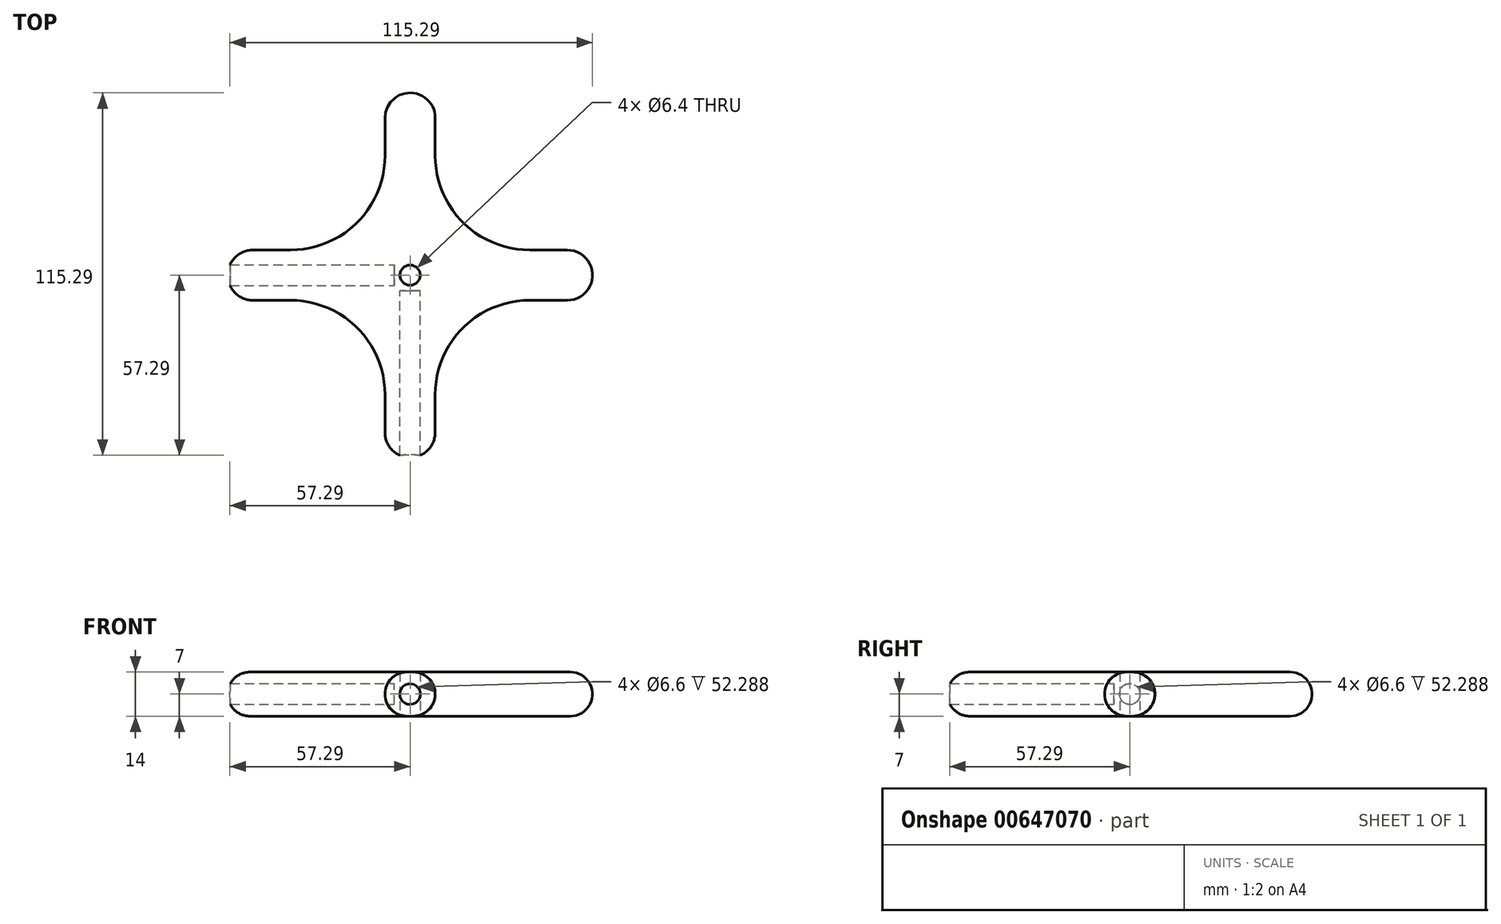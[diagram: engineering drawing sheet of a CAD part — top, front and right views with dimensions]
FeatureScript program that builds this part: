
annotation { "Feature Type Name" : "Feature", "Feature Type Description" : "" }
export const myFeature = defineFeature(function(context is Context, id is Id, definition is map)
    precondition{}
    {
        {
            var Q0;
            Q0=qCreatedBy(makeId("Top.planeOp"),FACE);
            var sketch = newSketch(context, id + "F0", { "sketchPlane" : qUnion([Q0])});
            skCircle(sketch, "E0", {"center": v(0, 0) * mm, "radius": 3.2 * mm});
            skLineSegment(sketch, "E1", {"start": v(0, 58) * mm, "end": v(0, 58) * mm});
            skLineSegment(sketch, "E2", {"start": v(-8, 50) * mm, "end": v(-8, 38) * mm});
            skLineSegment(sketch, "E3", {"start": v(-38, 8) * mm, "end": v(-50, 8) * mm});
            skLineSegment(sketch, "E4", {"start": v(-58, 0) * mm, "end": v(-58, 0) * mm});
            skPoint(sketch, "E5.visualSharp", {"position": v(-8, 8) * mm});
            skArc(sketch, "E5.filletArc", {"start": v(-38, 8) * mm, "mid": v(-16.79, 16.79) * mm, "end": v(-8, 38) * mm});
            skPoint(sketch, "E6.visualSharp", {"position": v(-8, 58) * mm});
            skArc(sketch, "E6.filletArc", {"start": v(0, 58) * mm, "mid": v(-5.66, 55.66) * mm, "end": v(-8, 50) * mm});
            skPoint(sketch, "E7.visualSharp", {"position": v(-58, 8) * mm});
            skArc(sketch, "E7.filletArc", {"start": v(-50, 8) * mm, "mid": v(-55.66, 5.66) * mm, "end": v(-58, 0) * mm});
            skLineSegment(sketch, "E8.MirrorCS", {"start": v(8, 50) * mm, "end": v(8, 38) * mm});
            skArc(sketch, "E9.MirrorCS", {"start": v(38, 8) * mm, "mid": v(16.79, 16.79) * mm, "end": v(8, 38) * mm});
            skArc(sketch, "E10.MirrorCS", {"start": v(0, 58) * mm, "mid": v(5.66, 55.66) * mm, "end": v(8, 50) * mm});
            skLineSegment(sketch, "E11.MirrorCS", {"start": v(38, 8) * mm, "end": v(50, 8) * mm});
            skArc(sketch, "E12.MirrorCS", {"start": v(50, 8) * mm, "mid": v(55.66, 5.66) * mm, "end": v(58, 0) * mm});
            skArc(sketch, "E13.MirrorCS", {"start": v(50, -8) * mm, "mid": v(55.66, -5.66) * mm, "end": v(58, 0) * mm});
            skLineSegment(sketch, "E14.MirrorCS", {"start": v(38, -8) * mm, "end": v(50, -8) * mm});
            skArc(sketch, "E15.MirrorCS", {"start": v(38, -8) * mm, "mid": v(16.79, -16.79) * mm, "end": v(8, -38) * mm});
            skLineSegment(sketch, "E16.MirrorCS", {"start": v(8, -50) * mm, "end": v(8, -38) * mm});
            skArc(sketch, "E17.MirrorCS", {"start": v(0, -58) * mm, "mid": v(5.66, -55.66) * mm, "end": v(8, -50) * mm});
            skArc(sketch, "E18.MirrorCS", {"start": v(0, -58) * mm, "mid": v(-5.66, -55.66) * mm, "end": v(-8, -50) * mm});
            skLineSegment(sketch, "E19.MirrorCS", {"start": v(-8, -50) * mm, "end": v(-8, -38) * mm});
            skArc(sketch, "E20.MirrorCS", {"start": v(-38, -8) * mm, "mid": v(-16.79, -16.79) * mm, "end": v(-8, -38) * mm});
            skLineSegment(sketch, "E21.MirrorCS", {"start": v(-38, -8) * mm, "end": v(-50, -8) * mm});
            skArc(sketch, "E22.MirrorCS", {"start": v(-50, -8) * mm, "mid": v(-55.66, -5.66) * mm, "end": v(-58, 0) * mm});
            skCircle(sketch, "E23", {"center": v(0, 0) * mm, "radius": 30 * mm, "construction": true});
            skSolve(sketch);
        }
        {
            var Q0;
            Q0=makeQuery(id+"F0.imprint","IMPRINT",FACE,{"disambiguationData":[TD([[makeQuery(id+"F0.imprint","IMPRINT",EDGE,{"derivedFrom":sQuery(id+"F0.wireOp",EDGE,"E0")}),-1.0]])]});
            extrude(context, id + "F1", {"entities" : qUnion([Q0]), "depth" : 14 * mm, "offsetDistance" : 25 * mm});
        }
        {
            var Q0;
            Q0=makeQuery(id+"F1.opExtrude","CAP_EDGE",EDGE,{"disambiguationData":[OSD([sQuery(id+"F0.wireOp",EDGE,"E5.filletArc")])],"isStart":false});
            fillet(context, id + "F2", {"entities" : qUnion([Q0]), "radius" : 7 * mm, "tangentPropagation" : true, "allowEdgeOverflow" : false});
        }
        {
            var Q0;
            Q0=makeQuery(id+"F1.opExtrude","CAP_EDGE",EDGE,{"disambiguationData":[OSD([sQuery(id+"F0.wireOp",EDGE,"E9.MirrorCS")])],"isStart":true});
            fillet(context, id + "F3", {"entities" : qUnion([Q0]), "radius" : 7 * mm, "tangentPropagation" : true, "allowEdgeOverflow" : false});
        }
        {
            var Q0;
            Q0=qCreatedBy(makeId("Front.planeOp"),FACE);
            var sketch = newSketch(context, id + "F4", { "sketchPlane" : qUnion([Q0])});
            skCircle(sketch, "E24", {"center": v(0, 7) * mm, "radius": 3.3 * mm});
            skSolve(sketch);
        }
        {
            var Q0;
            Q0=makeQuery(id+"F4.imprint","IMPRINT",FACE,{"disambiguationData":[TD([[makeQuery(id+"F4.imprint","IMPRINT",EDGE,{"derivedFrom":sQuery(id+"F4.wireOp",EDGE,"E24")}),1.0]])]});
            extrude(context, id + "F5", {"entities" : qUnion([Q0]), "operationType" : NewBodyOperationType.REMOVE, "depth" : 65 * mm, "offsetDistance" : 25 * mm, "hasSecondDirection" : true, "secondDirectionOppositeDirection" : false, "secondDirectionDepth" : 5 * mm});
        }
        {
            var Q0;
            Q0=qCreatedBy(makeId("Right.planeOp"),FACE);
            var sketch = newSketch(context, id + "F6", { "sketchPlane" : qUnion([Q0])});
            skCircle(sketch, "E25", {"center": v(0, 7) * mm, "radius": 3.3 * mm});
            skSolve(sketch);
        }
        {
            var Q0;
            Q0=makeQuery(id+"F6.imprint","IMPRINT",FACE,{"disambiguationData":[TD([[makeQuery(id+"F6.imprint","IMPRINT",EDGE,{"derivedFrom":sQuery(id+"F6.wireOp",EDGE,"E25")}),1.0]])]});
            extrude(context, id + "F7", {"entities" : qUnion([Q0]), "operationType" : NewBodyOperationType.REMOVE, "oppositeDirection" : true, "depth" : 65 * mm, "offsetDistance" : 25 * mm, "hasSecondDirection" : true, "secondDirectionOppositeDirection" : true, "secondDirectionDepth" : 5 * mm});
        }
    });
